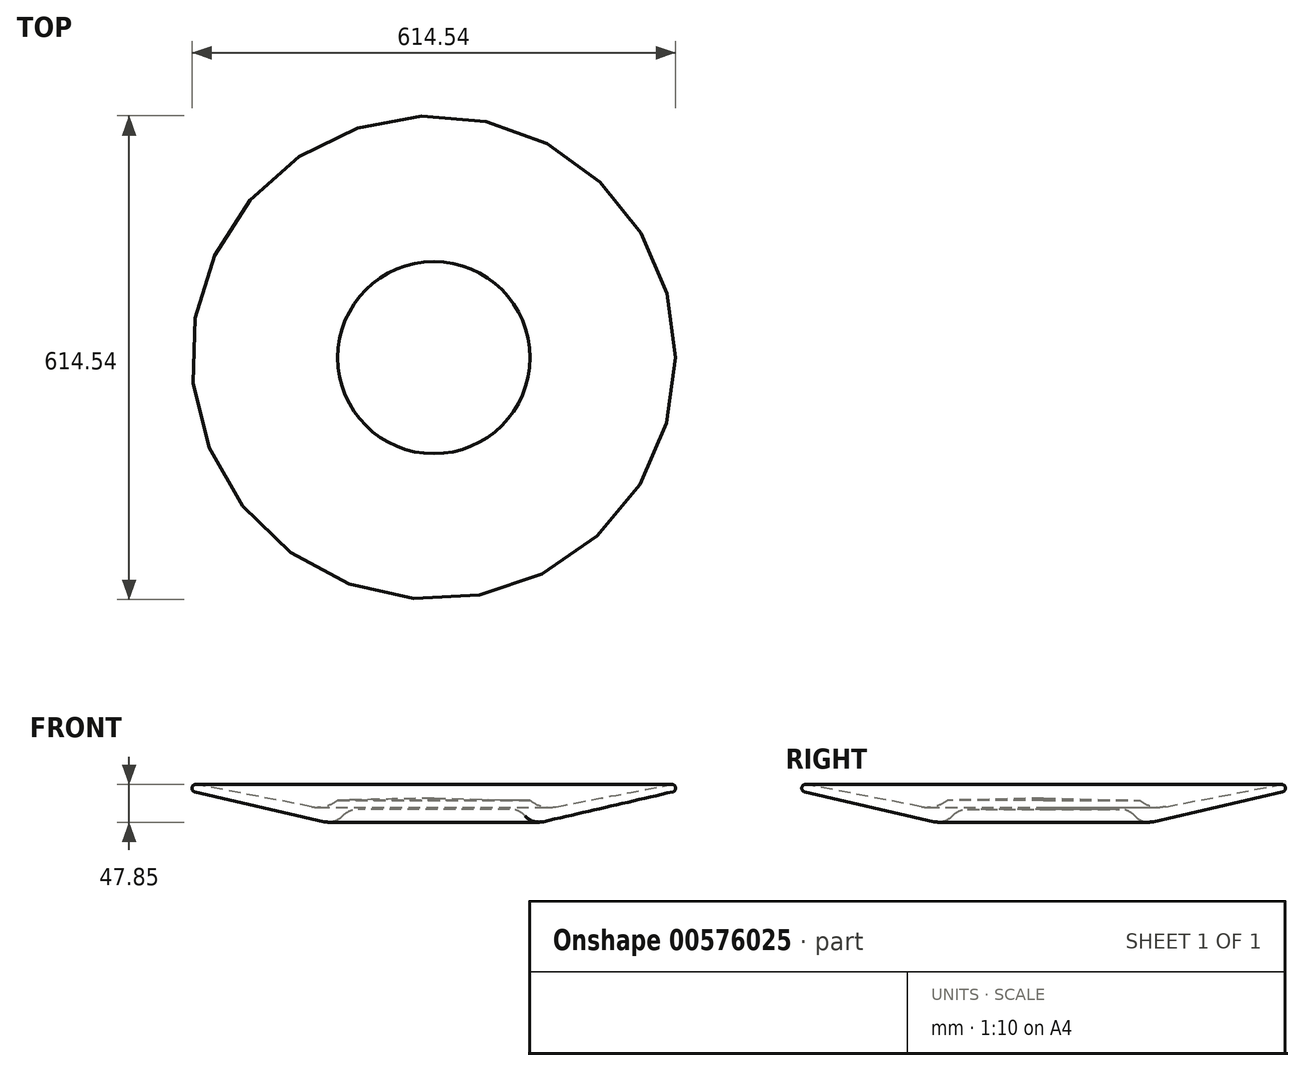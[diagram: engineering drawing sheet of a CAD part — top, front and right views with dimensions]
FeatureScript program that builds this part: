
annotation { "Feature Type Name" : "Feature", "Feature Type Description" : "" }
export const myFeature = defineFeature(function(context is Context, id is Id, definition is map)
    precondition{}
    {
        {
            var Q0;
            Q0=qCreatedBy(makeId("Front.planeOp"),FACE);
            var sketch = newSketch(context, id + "F0", { "sketchPlane" : qUnion([Q0])});
            skLineSegment(sketch, "E0", {"start": v(29.17, 96.53) * mm, "end": v(29.17, -95.3) * mm, "construction": true});
            skLineSegment(sketch, "E1", {"start": v(29.17, 13.97) * mm, "end": v(29.17, 0) * mm});
            skLineSegment(sketch, "E2", {"start": v(29.17, 0) * mm, "end": v(125.65, 0) * mm});
            skArc(sketch, "E3", {"start": v(145.1, -8.57) * mm, "mid": v(136.27, -2.24) * mm, "end": v(125.65, 0) * mm});
            skArc(sketch, "E4", {"start": v(145.1, -8.57) * mm, "mid": v(155.77, -15.35) * mm, "end": v(168.42, -15.82) * mm});
            skLineSegment(sketch, "E5", {"start": v(168.42, -15.82) * mm, "end": v(332.78, 22.1) * mm});
            skArc(sketch, "E6", {"start": v(332.78, 22.1) * mm, "mid": v(336.33, 27.68) * mm, "end": v(330.8, 31.32) * mm});
            skLineSegment(sketch, "E7", {"start": v(330.8, 31.32) * mm, "end": v(184.3, 3.14) * mm});
            skPoint(sketch, "E7.endSnap0", {"position": v(250.6, 3.14) * mm});
            skArc(sketch, "E8", {"start": v(151.25, 11.25) * mm, "mid": v(166.89, 3.58) * mm, "end": v(184.3, 3.14) * mm});
            skLineSegment(sketch, "E9", {"start": v(151.25, 11.25) * mm, "end": v(29.17, 13.97) * mm});
            skSolve(sketch);
        }
        {
            var Q0;
            Q0 = qSketchRegion(id + "F0", true);
            var Q1;
            Q1=sQuery(id+"F0.wireOp",EDGE,"E0");
            revolve(context, id + "F1", {"entities" : qUnion([Q0]), "axis" : qUnion([Q1]), "revolveType" : RevolveType.FULL});
        }
    });
